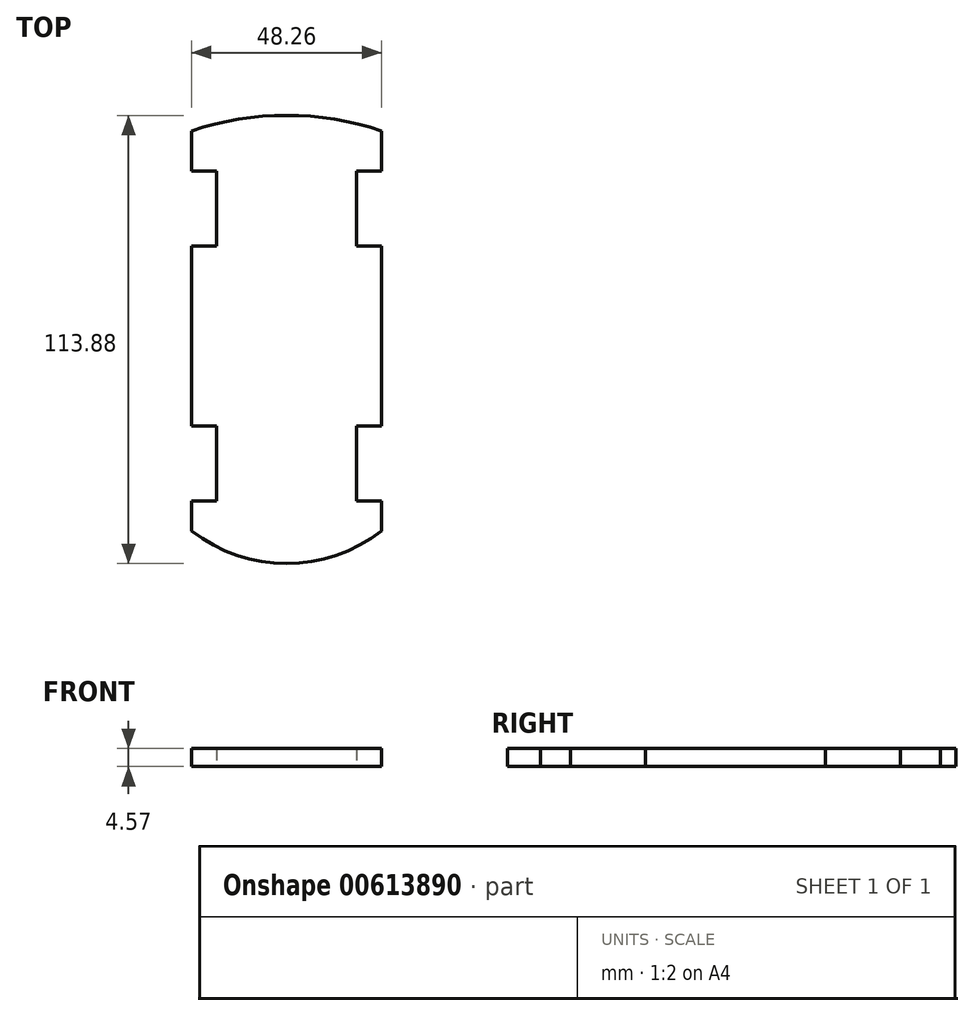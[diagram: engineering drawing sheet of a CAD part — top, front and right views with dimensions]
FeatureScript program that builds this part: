
annotation { "Feature Type Name" : "Feature", "Feature Type Description" : "" }
export const myFeature = defineFeature(function(context is Context, id is Id, definition is map)
    precondition{}
    {
        {
            var Q0;
            Q0=qCreatedBy(makeId("Top.planeOp"),FACE);
            var sketch = newSketch(context, id + "F0", { "sketchPlane" : qUnion([Q0])});
            skLineSegment(sketch, "E0", {"start": v(-54.85, 49.07) * mm, "end": v(-54.85, 38.91) * mm});
            skLineSegment(sketch, "E1", {"start": v(-54.85, 38.91) * mm, "end": v(-48.5, 38.91) * mm});
            skLineSegment(sketch, "E2", {"start": v(-48.5, 38.91) * mm, "end": v(-48.5, 19.86) * mm});
            skLineSegment(sketch, "E3", {"start": v(-48.5, 19.86) * mm, "end": v(-54.85, 19.86) * mm});
            skLineSegment(sketch, "E4", {"start": v(-54.85, 19.86) * mm, "end": v(-54.85, -25.86) * mm});
            skLineSegment(sketch, "E5", {"start": v(-54.85, -25.86) * mm, "end": v(-48.5, -25.86) * mm});
            skLineSegment(sketch, "E6", {"start": v(-48.5, -25.86) * mm, "end": v(-48.5, -44.9) * mm});
            skLineSegment(sketch, "E7", {"start": v(-48.5, -44.9) * mm, "end": v(-54.85, -44.9) * mm});
            skLineSegment(sketch, "E8", {"start": v(-54.85, -44.9) * mm, "end": v(-54.85, -52.53) * mm});
            skArc(sketch, "E9", {"start": v(-54.85, -52.53) * mm, "mid": v(-30.72, -60.85) * mm, "end": v(-6.6, -52.53) * mm});
            skArc(sketch, "E10", {"start": v(-6.6, 49.07) * mm, "mid": v(-30.72, 53.03) * mm, "end": v(-54.85, 49.07) * mm});
            skLineSegment(sketch, "E11", {"start": v(-6.6, 49.07) * mm, "end": v(-6.6, 38.91) * mm});
            skLineSegment(sketch, "E12", {"start": v(-6.6, 38.91) * mm, "end": v(-12.94, 38.91) * mm});
            skLineSegment(sketch, "E13", {"start": v(-12.94, 38.91) * mm, "end": v(-12.94, 19.86) * mm});
            skLineSegment(sketch, "E14", {"start": v(-12.94, 19.86) * mm, "end": v(-6.6, 19.86) * mm});
            skLineSegment(sketch, "E15", {"start": v(-6.6, 19.86) * mm, "end": v(-6.6, -25.86) * mm});
            skLineSegment(sketch, "E16", {"start": v(-6.6, -25.86) * mm, "end": v(-12.94, -25.86) * mm});
            skLineSegment(sketch, "E17", {"start": v(-12.94, -25.86) * mm, "end": v(-12.94, -44.9) * mm});
            skLineSegment(sketch, "E18", {"start": v(-12.94, -44.9) * mm, "end": v(-6.6, -44.9) * mm});
            skLineSegment(sketch, "E19", {"start": v(-6.6, -44.9) * mm, "end": v(-6.6, -52.53) * mm});
            skSolve(sketch);
        }
        {
            var Q0;
            Q0=makeQuery(id+"F0.imprint","IMPRINT",FACE,{"disambiguationData":[TD([[makeQuery(id+"F0.imprint","IMPRINT",EDGE,{"derivedFrom":sQuery(id+"F0.wireOp",EDGE,"E0")}),1.0]])]});
            extrude(context, id + "F1", {"entities" : qUnion([Q0]), "depth" : 4.57 * mm, "offsetDistance" : 25.4 * mm});
        }
    });
